# Revit family: S90-LINE BL 3000 DALI 830 MP_Unhosted
name_source: partatom
category: Lighting Fixtures
revit_build: Autodesk Revit 2016 (Build: 20161004_0715(x64)
units: mm (PartAtom-declared; Revit-internal decimal feet)

## family parameters
Always vertical = Yes
Cut with Voids When Loaded = No
Light Source = Yes
OmniClass Number = 23.80.70.00
OmniClass Title = Lighting
Part Type = Normal
Room Calculation Point = No
Round Connector Dimension = Use Diameter
Shared = No
Work Plane-Based = No

## types (1)
- S90-LINE BL 3000 DALI 830 MP_Unhosted
    # ballast on a MCB16 type B fuse = 24
    #Ballast = 1
    #Tubes = 1
    Apparent Load = 30 VA
    ArticleNumber = S90325530
    Body Material and Colour = Default
    Color Filter = 16777215
    Description = S90-LINE BL 3000 DALI 830 MP
    Dimming Lamp Color Temperature Shift = <None>
    EANNo = 7020940421249
    Emit Shape Visible in Rendering = Yes
    Emit from Rectangle Length = 53 mm  [stored 0.173885 ft]
    Emit from Rectangle Width = 1120 mm  [stored 3.67454 ft]
    Expired = 0
    Glamox Category = Interior
    Glamox Family = S90-LINE
    Glamox Mounting = Surface
    GlobalTradeItemNumber = 7020940421249
    Height = 86 mm  [stored 0.282152 ft]
    IFC Classification = Light Fixture
    IPClass = 20
    IP_Code = 20
    Lamp = LED
    Length = 1145 mm  [stored 3.75656 ft]
    LightFixtureMountingType = TRACKMOUNTED
    LightFixturePlacingType = CEILING
    LumLength = 1120 mm  [stored 3.67454 ft]
    LumWidth = 53 mm  [stored 0.173885 ft]
    MFArtNo = S90325530
    MaintenanceFactor = 0
    Manufacturer = Glamox
    Material LightingSurface = Material LightingSurface
    ModelLabel = S90-LINE BL 3000 DALI 830 MP
    ModelReference = S90-LINE
    Number of Poles = 1
    NumberOfSources = 1
    Optic = MP
    Photometric Web File = S90-LINE-3000-DALI-830-MP.ies
    Power Factor = 0.98
    PowerFactor = 98.00%
    Specification = Interior product, in bodymaterial Aluminium, for Surface/Track mounting, in Black colour, IP20, lightsource LED, lumen out 3130lm, ballast type DALI, optic type MP = Micro-Prismatic, gives an up/down lightdistribution 0/100.
    Suspension Material = Default
    Tilt Angle = 90.00°
    Total Load = 29 W
    TotalWattage = 29 W
    TypeOfBallast = DALI
    URL Denmark = http://glamox.com
    URL Estonia = http://glamox.com
    URL Finland = http://glamox.com
    URL Germany = http://glamox.com
    URL Ireland = http://glamox.com
    URL Norway = http://glamox.com
    URL Other = http://glamox.com
    URL Russia = http://glamox.com
    URL Sweden = http://glamox.com
    URL UK = http://glamox.com
    UpdateDate = 14.10.2020 22:57:35
    Voltage = 230 V
    Width = 66 mm  [stored 0.216535 ft]

note: [stored X ft] marks values corroborated as IEEE doubles in the binary element streams (Revit-internal decimal feet)

## geometry (parser evidence)
native form markers: Sweep x3
no freeform markers — native parametric forms only
